# Revit family: PRD_FrankeWS_HldrsAndHks_DoubleClothHook_CHRX690
name_source: partatom
category: Specialty Equipment
revit_build: Autodesk Revit 2018 (Build: 20190510_1515(x64)
units: mm (PartAtom-declared; Revit-internal decimal feet)

## family parameters
Cut with Voids When Loaded = No
Host = Face
OmniClass Number = 23.40.20.21
OmniClass Title = Toilet and Bath Specialties
Part Type = Normal
Room Calculation Point = No
Round Connector Dimension = Use Diameter
Shared = No

## types (1)
- CHRX690
    AssetType = Fixed
    BIMObjectName = PRD_AR_HoldersAndHooks_DoubleClothHook_CHRX690
    Category = Pr_30_36_59_38, Holders and hooks
    Default Elevation = 1600 mm  [stored 5.24934 ft]
    Description = Double cloth hook for wall mounting, stainless steel, surface satin finished, two drilled holes for fixation, includes stainless steel screws and dowels.
    DurationUnit = year
    Features = stainless steel, included fixing material
    Finish = satin finished
    GrossWeight = 0.25 kg
    HookMaterial = PRD_AR_StainlessSteel_SatinFinished
    IfcExportAs = IfcFurnitureType
    IfcExportType = USERDEFINED
    IsBuiltIn = TRUE
    MainColor = stainless steel
    Manufacturer = KWC Group AG
    ManufacturerName = KWC Group AG
    ManufacturerURL = www.kwc.com
    Material = stainless steel
    MaterialCode = 1.4301
    MaterialThickness = 2.00 mm
    Model = CHRX690
    ModelNumber = 2000057150
    ModelReference = CHRX690
    NBSDescription = Holders and hooks
    NBSReference = 45-25-60/350
    Name = Double cloth hook CHRX690
    NetWeight = 0.25 kg
    NominalDepth = 100 mm  [stored 0.328084 ft]
    NominalHeight = 158 mm
    NominalWidth = 30 mm  [stored 0.0984252 ft]
    ProductInformation = https://pim.kwc.com
    Size = 30 x 158 x 100 mm
    Style = Hook
    TypeOfFixing = Screw
    TypeOfMounting = Wall mounting
    URL = www.kwc.com
    Uniclass2015Code = Pr_30_36_59_38
    Uniclass2015Title = Holders and hooks
    Uniclass2015Version = Products v1.10
    Version = 1
    WarrantyDurationUnit = year

note: [stored X ft] marks values corroborated as IEEE doubles in the binary element streams (Revit-internal decimal feet)

## geometry (parser evidence)
native form markers: Sweep x2
no freeform markers — native parametric forms only
